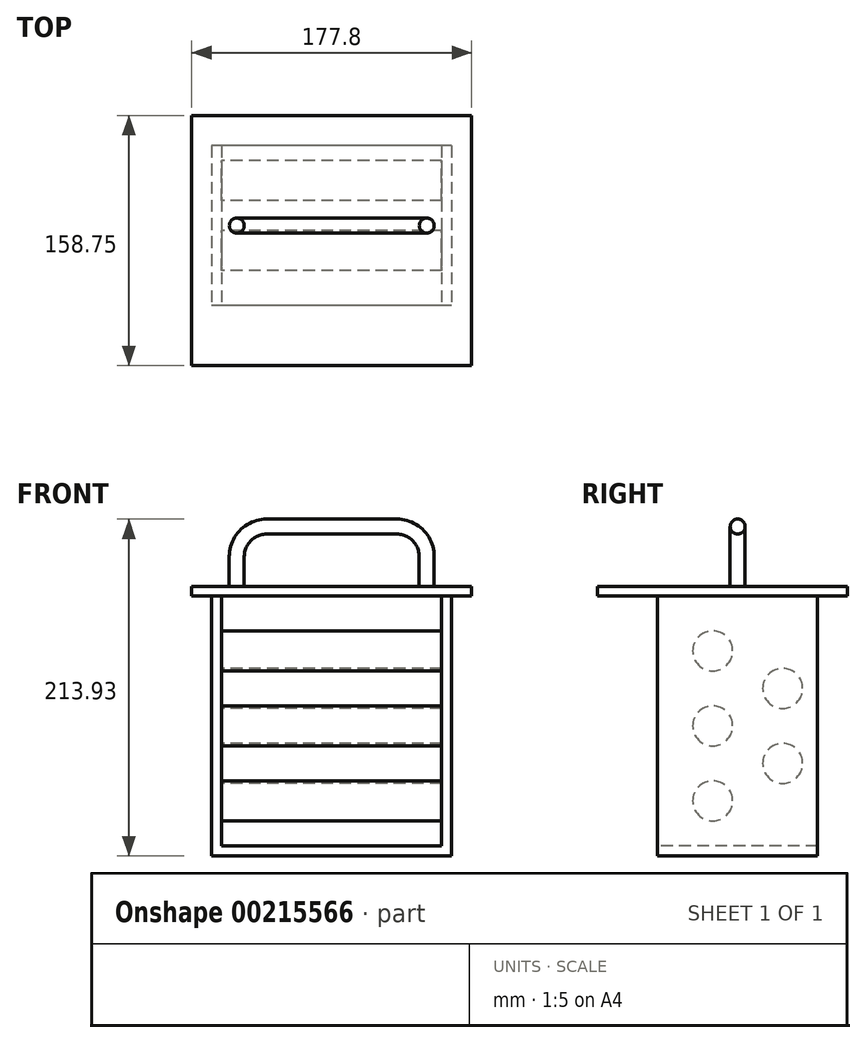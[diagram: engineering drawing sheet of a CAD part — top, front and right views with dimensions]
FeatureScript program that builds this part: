
annotation { "Feature Type Name" : "Feature", "Feature Type Description" : "" }
export const myFeature = defineFeature(function(context is Context, id is Id, definition is map)
    precondition{}
    {
        {
            var Q0;
            Q0=qCreatedBy(makeId("Right.planeOp"),FACE);
            var sketch = newSketch(context, id + "F0", { "sketchPlane" : qUnion([Q0])});
            skLineSegment(sketch, "E0.bottom", {"start": v(50.8, -82.55) * mm, "end": v(-50.8, -82.55) * mm});
            skLineSegment(sketch, "E0.top", {"start": v(50.8, 82.55) * mm, "end": v(-50.8, 82.55) * mm});
            skLineSegment(sketch, "E0.left", {"start": v(50.8, -82.55) * mm, "end": v(50.8, 82.55) * mm});
            skLineSegment(sketch, "E0.right", {"start": v(-50.8, -82.55) * mm, "end": v(-50.8, 82.55) * mm});
            skPoint(sketch, "E0.middle", {"position": v(0, 0) * mm});
            skLineSegment(sketch, "E1", {"start": v(-25.4, 82.55) * mm, "end": v(-25.4, -82.55) * mm, "construction": true});
            skLineSegment(sketch, "E2", {"start": v(25.4, 82.55) * mm, "end": v(25.4, -82.55) * mm, "construction": true});
            skLineSegment(sketch, "E3", {"start": v(-50.8, 57.15) * mm, "end": v(-25.4, 57.15) * mm, "construction": true});
            skLineSegment(sketch, "E4", {"start": v(-25.4, 0) * mm, "end": v(-50.8, 0) * mm, "construction": true});
            skLineSegment(sketch, "E5", {"start": v(-25.4, -57.15) * mm, "end": v(-50.8, -57.15) * mm, "construction": true});
            skLineSegment(sketch, "E6", {"start": v(25.4, 28.58) * mm, "end": v(50.8, 28.58) * mm, "construction": true});
            skLineSegment(sketch, "E7", {"start": v(25.4, -28.57) * mm, "end": v(50.8, -28.57) * mm, "construction": true});
            skCircle(sketch, "E8", {"center": v(-25.4, 57.15) * mm, "radius": 15.88 * mm});
            skCircle(sketch, "E9", {"center": v(-25.4, -57.15) * mm, "radius": 15.88 * mm});
            skCircle(sketch, "E10", {"center": v(-25.4, 0) * mm, "radius": 15.88 * mm});
            skCircle(sketch, "E11", {"center": v(25.4, 28.58) * mm, "radius": 15.88 * mm});
            skCircle(sketch, "E12", {"center": v(25.4, -28.57) * mm, "radius": 15.88 * mm});
            skLineSegment(sketch, "E13", {"start": v(-50.8, 82.55) * mm, "end": v(-88.9, 82.55) * mm});
            skLineSegment(sketch, "E14", {"start": v(-88.9, 82.55) * mm, "end": v(-88.9, 88.9) * mm});
            skLineSegment(sketch, "E15", {"start": v(-88.9, 88.9) * mm, "end": v(69.85, 88.9) * mm});
            skLineSegment(sketch, "E16", {"start": v(69.85, 88.9) * mm, "end": v(69.85, 82.55) * mm});
            skLineSegment(sketch, "E17", {"start": v(69.85, 82.55) * mm, "end": v(50.8, 82.55) * mm});
            skSolve(sketch);
        }
        {
            var Q0;
            Q0=makeQuery(id+"F0.imprint","IMPRINT",FACE,{"disambiguationData":[TD([[makeQuery(id+"F0.imprint","IMPRINT",EDGE,{"derivedFrom":sQuery(id+"F0.wireOp",EDGE,"E0.bottom")}),-1.0]])]});
            var Q1;
            Q1=makeQuery(id+"F0.imprint","IMPRINT",FACE,{"disambiguationData":[TD([[makeQuery(id+"F0.imprint","IMPRINT",EDGE,{"derivedFrom":sQuery(id+"F0.wireOp",EDGE,"E8")}),1.0]])]});
            var Q2;
            Q2=makeQuery(id+"F0.imprint","IMPRINT",FACE,{"disambiguationData":[TD([[makeQuery(id+"F0.imprint","IMPRINT",EDGE,{"derivedFrom":sQuery(id+"F0.wireOp",EDGE,"E11")}),1.0]])]});
            var Q3;
            Q3=makeQuery(id+"F0.imprint","IMPRINT",FACE,{"disambiguationData":[TD([[makeQuery(id+"F0.imprint","IMPRINT",EDGE,{"derivedFrom":sQuery(id+"F0.wireOp",EDGE,"E10")}),1.0]])]});
            var Q4;
            Q4=makeQuery(id+"F0.imprint","IMPRINT",FACE,{"disambiguationData":[TD([[makeQuery(id+"F0.imprint","IMPRINT",EDGE,{"derivedFrom":sQuery(id+"F0.wireOp",EDGE,"E12")}),1.0]])]});
            var Q5;
            Q5=makeQuery(id+"F0.imprint","IMPRINT",FACE,{"disambiguationData":[TD([[makeQuery(id+"F0.imprint","IMPRINT",EDGE,{"derivedFrom":sQuery(id+"F0.wireOp",EDGE,"E9")}),1.0]])]});
            extrude(context, id + "F1", {"entities" : qUnion([Q0, Q1, Q2, Q3, Q4, Q5]), "endBound" : BoundingType.SYMMETRIC, "depth" : 152.4 * mm});
        }
        {
            var Q0;
            Q0=makeQuery(id+"F1.opExtrude","SWEPT_FACE",FACE,{"disambiguationData":[OSD([sQuery(id+"F0.wireOp",EDGE,"E0.right")])]});
            var sketch = newSketch(context, id + "F2", { "sketchPlane" : qUnion([Q0])});
            skLineSegment(sketch, "E18.bottom", {"start": v(69.85, -76.2) * mm, "end": v(-69.85, -76.2) * mm});
            skLineSegment(sketch, "E18.left", {"start": v(69.85, -76.2) * mm, "end": v(69.85, 82.55) * mm});
            skLineSegment(sketch, "E18.right", {"start": v(-69.85, -76.2) * mm, "end": v(-69.85, 82.55) * mm});
            skPoint(sketch, "E18.middle", {"position": v(0, 0) * mm});
            skLineSegment(sketch, "E19.0", {"start": v(76.2, 82.55) * mm, "end": v(-76.2, 82.55) * mm});
            skPoint(sketch, "E20.orphan", {"position": v(-69.85, 76.2) * mm});
            skPoint(sketch, "E21.orphan", {"position": v(69.85, 76.2) * mm});
            skSolve(sketch);
        }
        {
            var Q0;
            Q0=makeQuery(id+"F2.imprint","IMPRINT",FACE,{"disambiguationData":[TD([[makeQuery(id+"F2.imprint","IMPRINT",EDGE,{"derivedFrom":sQuery(id+"F2.wireOp",EDGE,"E18.bottom")}),-1.0]])]});
            extrude(context, id + "F3", {"entities" : qUnion([Q0]), "operationType" : NewBodyOperationType.REMOVE, "endBound" : BoundingType.THROUGH_ALL, "oppositeDirection" : true, "depth" : 25.4 * mm});
        }
        {
            var Q0;
            Q0=qCreatedBy(makeId("Right.planeOp"),FACE);
            var sketch = newSketch(context, id + "F4", { "sketchPlane" : qUnion([Q0])});
            skLineSegment(sketch, "E22.bottom", {"start": v(50.8, -82.55) * mm, "end": v(-50.8, -82.55) * mm});
            skLineSegment(sketch, "E22.top", {"start": v(50.8, 82.55) * mm, "end": v(-50.8, 82.55) * mm});
            skLineSegment(sketch, "E22.left", {"start": v(50.8, -82.55) * mm, "end": v(50.8, 82.55) * mm});
            skLineSegment(sketch, "E22.right", {"start": v(-50.8, -82.55) * mm, "end": v(-50.8, 82.55) * mm});
            skPoint(sketch, "E22.middle", {"position": v(0, 0) * mm});
            skLineSegment(sketch, "E23", {"start": v(-15.88, 82.55) * mm, "end": v(-15.88, -82.55) * mm, "construction": true});
            skLineSegment(sketch, "E24", {"start": v(28.57, 82.55) * mm, "end": v(28.57, -82.55) * mm, "construction": true});
            skLineSegment(sketch, "E25", {"start": v(-50.8, 47.63) * mm, "end": v(-15.88, 47.63) * mm, "construction": true});
            skLineSegment(sketch, "E26", {"start": v(-15.88, 0) * mm, "end": v(-50.8, 0) * mm, "construction": true});
            skLineSegment(sketch, "E27", {"start": v(-15.88, -47.63) * mm, "end": v(-50.8, -47.63) * mm, "construction": true});
            skLineSegment(sketch, "E28", {"start": v(28.57, 23.81) * mm, "end": v(50.8, 23.81) * mm, "construction": true});
            skLineSegment(sketch, "E29", {"start": v(28.57, -23.81) * mm, "end": v(50.8, -23.81) * mm, "construction": true});
            skCircle(sketch, "E30", {"center": v(-15.88, 47.63) * mm, "radius": 12.7 * mm});
            skCircle(sketch, "E31", {"center": v(-15.88, -47.63) * mm, "radius": 12.7 * mm});
            skCircle(sketch, "E32", {"center": v(-15.88, 0) * mm, "radius": 12.7 * mm});
            skCircle(sketch, "E33", {"center": v(28.57, 23.81) * mm, "radius": 12.7 * mm});
            skCircle(sketch, "E34", {"center": v(28.57, -23.81) * mm, "radius": 12.7 * mm});
            skLineSegment(sketch, "E35", {"start": v(-50.8, 82.55) * mm, "end": v(-88.9, 82.55) * mm});
            skLineSegment(sketch, "E36", {"start": v(-88.9, 82.55) * mm, "end": v(-88.9, 88.52) * mm});
            skLineSegment(sketch, "E37", {"start": v(-88.9, 88.52) * mm, "end": v(63.5, 88.52) * mm});
            skLineSegment(sketch, "E38", {"start": v(63.5, 88.52) * mm, "end": v(63.5, 82.55) * mm});
            skLineSegment(sketch, "E39", {"start": v(63.5, 82.55) * mm, "end": v(50.8, 82.55) * mm});
            skSolve(sketch);
        }
        {
            var Q0;
            Q0=makeQuery(id+"F4.imprint","IMPRINT",FACE,{"disambiguationData":[TD([[makeQuery(id+"F4.imprint","IMPRINT",EDGE,{"derivedFrom":sQuery(id+"F4.wireOp",EDGE,"E30")}),1.0]])]});
            var Q1;
            Q1=makeQuery(id+"F4.imprint","IMPRINT",FACE,{"disambiguationData":[TD([[makeQuery(id+"F4.imprint","IMPRINT",EDGE,{"derivedFrom":sQuery(id+"F4.wireOp",EDGE,"E33")}),1.0]])]});
            var Q2;
            Q2=makeQuery(id+"F4.imprint","IMPRINT",FACE,{"disambiguationData":[TD([[makeQuery(id+"F4.imprint","IMPRINT",EDGE,{"derivedFrom":sQuery(id+"F4.wireOp",EDGE,"E32")}),1.0]])]});
            var Q3;
            Q3=makeQuery(id+"F4.imprint","IMPRINT",FACE,{"disambiguationData":[TD([[makeQuery(id+"F4.imprint","IMPRINT",EDGE,{"derivedFrom":sQuery(id+"F4.wireOp",EDGE,"E34")}),1.0]])]});
            var Q4;
            Q4=makeQuery(id+"F4.imprint","IMPRINT",FACE,{"disambiguationData":[TD([[makeQuery(id+"F4.imprint","IMPRINT",EDGE,{"derivedFrom":sQuery(id+"F4.wireOp",EDGE,"E31")}),1.0]])]});
            extrude(context, id + "F5", {"entities" : qUnion([Q0, Q1, Q2, Q3, Q4]), "operationType" : NewBodyOperationType.ADD, "endBound" : BoundingType.SYMMETRIC, "depth" : 146.05 * mm});
        }
        {
            var Q0;
            Q0=qCreatedBy(makeId("Right.planeOp"),FACE);
            var sketch = newSketch(context, id + "F6", { "sketchPlane" : qUnion([Q0])});
            skLineSegment(sketch, "E40.0", {"start": v(50.8, 82.55) * mm, "end": v(-50.8, 82.55) * mm});
            skLineSegment(sketch, "E41", {"start": v(-50.8, 82.55) * mm, "end": v(-88.9, 82.55) * mm});
            skLineSegment(sketch, "E42", {"start": v(-88.9, 82.55) * mm, "end": v(-88.9, 88.52) * mm});
            skLineSegment(sketch, "E43", {"start": v(-88.9, 88.52) * mm, "end": v(69.85, 88.52) * mm});
            skLineSegment(sketch, "E44", {"start": v(69.85, 88.52) * mm, "end": v(69.85, 82.55) * mm});
            skLineSegment(sketch, "E45", {"start": v(69.85, 82.55) * mm, "end": v(50.8, 82.55) * mm});
            skSolve(sketch);
        }
        {
            var Q0;
            Q0 = qSketchRegion(id + "F6", true);
            extrude(context, id + "F7", {"entities" : qUnion([Q0]), "operationType" : NewBodyOperationType.ADD, "endBound" : BoundingType.SYMMETRIC, "depth" : 177.8 * mm});
        }
        {
            var Q0;
            Q0=makeQuery(id+"F7.opExtrude","SWEPT_FACE",FACE,{"disambiguationData":[OSD([sQuery(id+"F6.wireOp",EDGE,"E43")])]});
            var sketch = newSketch(context, id + "F8", { "sketchPlane" : qUnion([Q0])});
            skCircle(sketch, "E46", {"center": v(-60.33, 0) * mm, "radius": 4.76 * mm});
            skCircle(sketch, "E47", {"center": v(60.33, 0) * mm, "radius": 4.76 * mm});
            skSolve(sketch);
        }
        {
            var Q0;
            Q0=qCreatedBy(makeId("Front.planeOp"),FACE);
            var sketch = newSketch(context, id + "F9", { "sketchPlane" : qUnion([Q0])});
            skPoint(sketch, "E48.0", {"position": v(-60.33, 88.52) * mm});
            skPoint(sketch, "E49.0", {"position": v(60.33, 88.52) * mm});
            skLineSegment(sketch, "E50", {"start": v(-60.33, 88.52) * mm, "end": v(-60.33, 107.57) * mm});
            skLineSegment(sketch, "E51", {"start": v(-41.28, 126.62) * mm, "end": v(41.28, 126.62) * mm});
            skLineSegment(sketch, "E52", {"start": v(60.33, 107.57) * mm, "end": v(60.33, 88.52) * mm});
            skPoint(sketch, "E53.visualSharp", {"position": v(-60.33, 126.62) * mm});
            skArc(sketch, "E53.filletArc", {"start": v(-41.28, 126.62) * mm, "mid": v(-54.75, 121.04) * mm, "end": v(-60.33, 107.57) * mm});
            skPoint(sketch, "E54.visualSharp", {"position": v(60.33, 126.62) * mm});
            skArc(sketch, "E54.filletArc", {"start": v(60.33, 107.57) * mm, "mid": v(54.75, 121.04) * mm, "end": v(41.28, 126.62) * mm});
            skSolve(sketch);
        }
        {
            var Q0;
            Q0=makeQuery(id+"F8.imprint","IMPRINT",FACE,{"disambiguationData":[TD([[makeQuery(id+"F8.imprint","IMPRINT",EDGE,{"derivedFrom":sQuery(id+"F8.wireOp",EDGE,"E46")}),1.0]])]});
            var Q1;
            Q1 = qConstructionFilter(qBodyType(qCreatedBy(id + "F9" ,EDGE), BodyType.WIRE), ConstructionObject.NO);
            sweep(context, id + "F10", {"operationType" : NewBodyOperationType.ADD, "profiles" : qUnion([Q0]), "path" : qUnion([Q1])});
        }
    });
